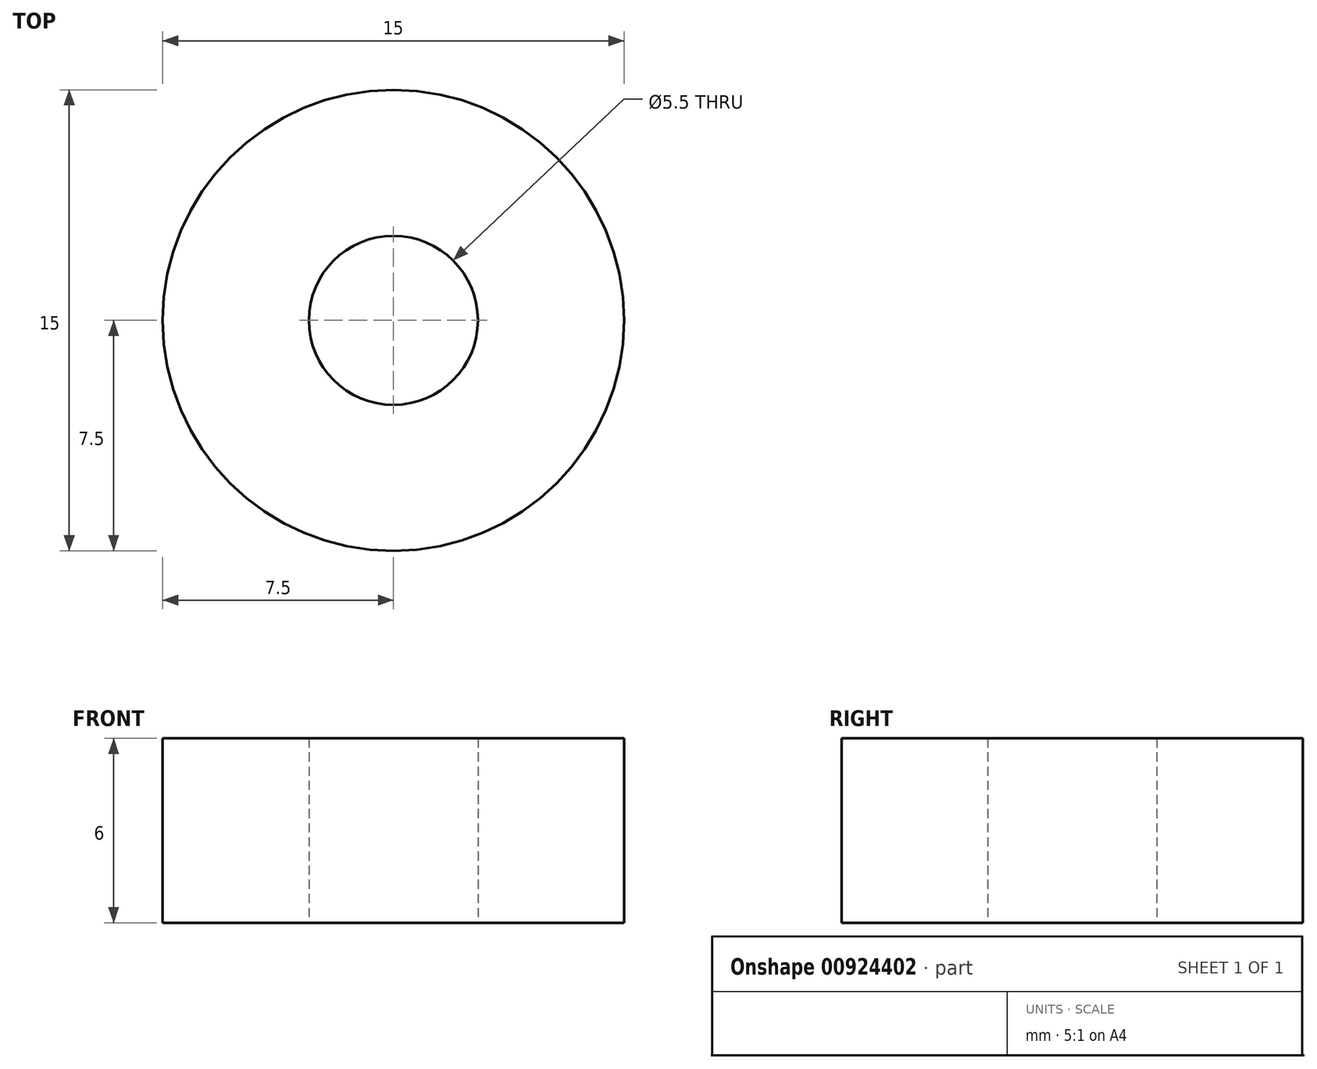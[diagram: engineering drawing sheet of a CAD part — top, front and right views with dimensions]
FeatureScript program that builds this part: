
annotation { "Feature Type Name" : "Feature", "Feature Type Description" : "" }
export const myFeature = defineFeature(function(context is Context, id is Id, definition is map)
    precondition{}
    {
        {
            var Q0;
            Q0=qCreatedBy(makeId("Top.planeOp"),FACE);
            var sketch = newSketch(context, id + "F0", { "sketchPlane" : qUnion([Q0])});
            skCircle(sketch, "E0", {"center": v(0, 0) * mm, "radius": 7.5 * mm});
            skCircle(sketch, "E1", {"center": v(0, 0) * mm, "radius": 2.75 * mm});
            skSolve(sketch);
        }
        {
            var Q0;
            Q0 = qSketchRegion(id + "F0", true);
            extrude(context, id + "F1", {"entities" : qUnion([Q0]), "depth" : 3 * mm, "offsetDistance" : 25 * mm, "hasSecondDirection" : true, "secondDirectionOppositeDirection" : true, "secondDirectionDepth" : 3 * mm});
        }
    });
